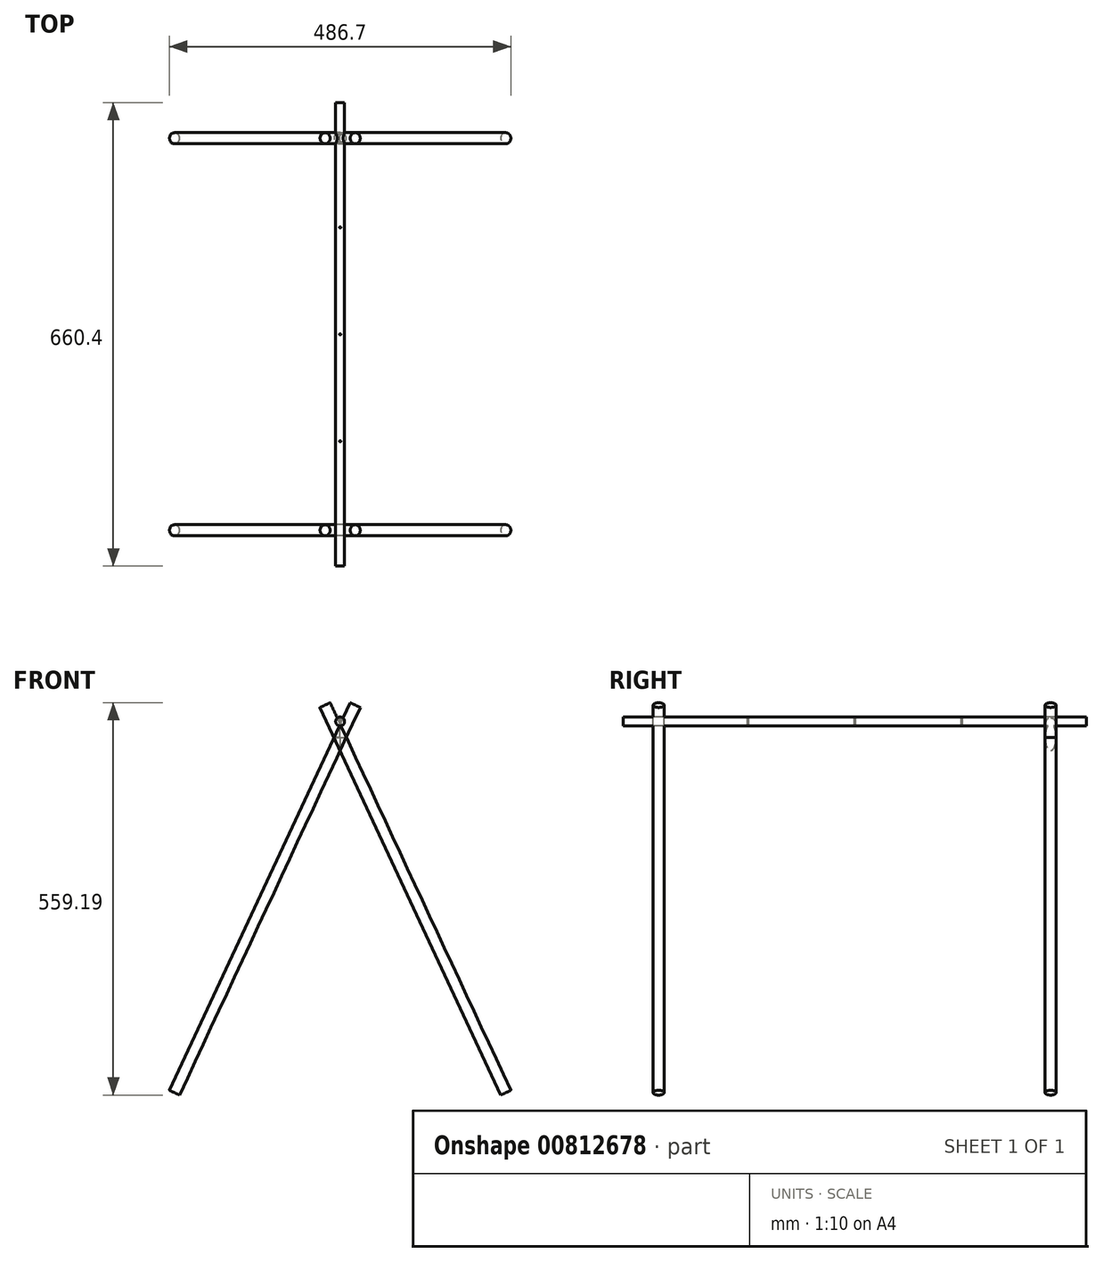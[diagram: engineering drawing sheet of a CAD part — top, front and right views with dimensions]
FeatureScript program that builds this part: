
annotation { "Feature Type Name" : "Feature", "Feature Type Description" : "" }
export const myFeature = defineFeature(function(context is Context, id is Id, definition is map)
    precondition{}
    {
        {
            var Q0;
            Q0=qCreatedBy(makeId("Front.planeOp"),FACE);
            var sketch = newSketch(context, id + "F0", { "sketchPlane" : qUnion([Q0])});
            skLineSegment(sketch, "E0", {"start": v(0, 0) * mm, "end": v(-236.16, -506.44) * mm});
            skLineSegment(sketch, "E1", {"start": v(0, 0) * mm, "end": v(236.16, -506.44) * mm});
            skLineSegment(sketch, "E2", {"start": v(0, 0) * mm, "end": v(21.47, 46.04) * mm});
            skLineSegment(sketch, "E3", {"start": v(0, 0) * mm, "end": v(-21.47, 46.04) * mm});
            skLineSegment(sketch, "E4.0", {"start": v(-7.2, 3.35) * mm, "end": v(-243.35, -503.1) * mm});
            skLineSegment(sketch, "E5.0", {"start": v(-7.2, 3.35) * mm, "end": v(14.28, 49.4) * mm});
            skLineSegment(sketch, "E6", {"start": v(14.28, 49.4) * mm, "end": v(21.47, 46.04) * mm});
            skLineSegment(sketch, "E7", {"start": v(-243.35, -503.1) * mm, "end": v(-236.16, -506.44) * mm});
            skLineSegment(sketch, "E8.0", {"start": v(7.2, 3.35) * mm, "end": v(243.35, -503.1) * mm});
            skLineSegment(sketch, "E9.0", {"start": v(7.2, 3.35) * mm, "end": v(-14.28, 49.4) * mm});
            skLineSegment(sketch, "E10", {"start": v(236.16, -506.44) * mm, "end": v(243.35, -503.1) * mm});
            skLineSegment(sketch, "E11", {"start": v(-21.47, 46.04) * mm, "end": v(-14.28, 49.4) * mm});
            skSolve(sketch);
        }
        {
            var Q0;
            {var subQ0=sQuery(id+"F0.wireOp",EDGE,"E2");Q0=makeQuery(id+"F0.imprint","IMPRINT",FACE,{"disambiguationData":[TD([[makeQuery(id+"F0.imprint","IMPRINT",EDGE,{"derivedFrom":subQ0}),1.0]])]});}
            var Q1;
            {var subQ0=sQuery(id+"F0.wireOp",EDGE,"E5.0");var subQ1=sQuery(id+"F0.wireOp",EDGE,"E4.0");var subQ2=makeQuery(id+"F0.imprint","INTERSECT",VERTEX,{"derivedFrom":[subQ1,subQ0]});Q1=makeQuery(id+"F0.imprint","IMPRINT",FACE,{"disambiguationData":[TD([[makeQuery(id+"F0.imprint","IMPRINT",EDGE,{"disambiguationData":[TD([[subQ2,-1.0]])],"derivedFrom":subQ1}),1.0]])]});}
            var Q2;
            {var subQ7=sQuery(id+"F0.wireOp",EDGE,"E7");Q2=makeQuery(id+"F0.imprint","IMPRINT",FACE,{"disambiguationData":[TD([[makeQuery(id+"F0.imprint","IMPRINT",EDGE,{"derivedFrom":subQ7}),1.0]])]});}
            var Q3;
            Q3=sQuery(id+"F0.wireOp",EDGE,"E0");
            revolve(context, id + "F1", {"surfaceOperationType" : NewSurfaceOperationType.NEW, "entities" : qUnion([Q0, Q1, Q2]), "axis" : qUnion([Q3]), "revolveType" : RevolveType.FULL});
        }
        {
            var Q0;
            {var subQ0=sQuery(id+"F0.wireOp",EDGE,"E11");Q0=makeQuery(id+"F0.imprint","IMPRINT",FACE,{"disambiguationData":[TD([[makeQuery(id+"F0.imprint","IMPRINT",EDGE,{"derivedFrom":subQ0}),-1.0]])]});}
            var Q1;
            {var subQ4=sQuery(id+"F0.wireOp",EDGE,"E1");Q1=makeQuery(id+"F0.imprint","IMPRINT",FACE,{"disambiguationData":[TD([[makeQuery(id+"F0.imprint","IMPRINT",EDGE,{"derivedFrom":subQ4}),1.0]])]});}
            var Q2;
            {var subQ0=sQuery(id+"F0.wireOp",EDGE,"E3");var subQ5=sQuery(id+"F0.wireOp",EDGE,"E5.0");var subQ6=makeQuery(id+"F0.imprint","INTERSECT",VERTEX,{"derivedFrom":[subQ0,subQ5]});Q2=makeQuery(id+"F0.imprint","IMPRINT",FACE,{"disambiguationData":[TD([[makeQuery(id+"F0.imprint","IMPRINT",EDGE,{"disambiguationData":[TD([[subQ6,-1.0]])],"derivedFrom":subQ5}),-1.0]])]});}
            var Q3;
            Q3=sQuery(id+"F0.wireOp",EDGE,"E1");
            revolve(context, id + "F2", {"surfaceOperationType" : NewSurfaceOperationType.NEW, "entities" : qUnion([Q0, Q1, Q2]), "axis" : qUnion([Q3]), "revolveType" : RevolveType.FULL});
        }
        {
            var Q0;
            Q0=qCreatedBy(makeId("Front.planeOp"),FACE);
            var sketch = newSketch(context, id + "F3", { "sketchPlane" : qUnion([Q0])});
            skLineSegment(sketch, "E12.0", {"start": v(7.2, 3.35) * mm, "end": v(-14.28, 49.4) * mm});
            skLineSegment(sketch, "E13.0", {"start": v(-7.2, 3.35) * mm, "end": v(14.28, 49.4) * mm});
            skLineSegment(sketch, "E14.0", {"start": v(0, 0) * mm, "end": v(21.47, 46.04) * mm});
            skLineSegment(sketch, "E15.0", {"start": v(0, 0) * mm, "end": v(-21.47, 46.04) * mm});
            skLineSegment(sketch, "E16", {"start": v(0, 18.78) * mm, "end": v(0, 22.75) * mm});
            skCircle(sketch, "E17", {"center": v(0, 22.75) * mm, "radius": 6.35 * mm});
            skSolve(sketch);
        }
        {
            var Q0;
            {var subQ0=sQuery(id+"F3.wireOp",EDGE,"E13.0");var subQ1=sQuery(id+"F3.wireOp",EDGE,"E12.0");var subQ2=makeQuery(id+"F3.imprint","INTERSECT",VERTEX,{"derivedFrom":[subQ1,subQ0]});Q0=makeQuery(id+"F3.imprint","IMPRINT",FACE,{"disambiguationData":[TD([[makeQuery(id+"F3.imprint","IMPRINT",EDGE,{"disambiguationData":[TD([[subQ2,-1.0]])],"derivedFrom":subQ1}),-1.0]])]});}
            var Q1;
            {var subQ0=sQuery(id+"F3.wireOp",EDGE,"E13.0");var subQ1=sQuery(id+"F3.wireOp",EDGE,"E12.0");var subQ2=makeQuery(id+"F3.imprint","INTERSECT",VERTEX,{"derivedFrom":[subQ1,subQ0]});Q1=makeQuery(id+"F3.imprint","IMPRINT",FACE,{"disambiguationData":[TD([[makeQuery(id+"F3.imprint","IMPRINT",EDGE,{"disambiguationData":[TD([[subQ2,1.0]])],"derivedFrom":subQ1}),-1.0]])]});}
            var Q2;
            {var subQ0=sQuery(id+"F3.wireOp",EDGE,"E13.0");var subQ1=sQuery(id+"F3.wireOp",EDGE,"E12.0");var subQ2=makeQuery(id+"F3.imprint","INTERSECT",VERTEX,{"derivedFrom":[subQ1,subQ0]});Q2=makeQuery(id+"F3.imprint","IMPRINT",FACE,{"disambiguationData":[TD([[makeQuery(id+"F3.imprint","IMPRINT",EDGE,{"disambiguationData":[TD([[subQ2,1.0]])],"derivedFrom":subQ1}),1.0]])]});}
            var Q3;
            {var subQ0=sQuery(id+"F3.wireOp",EDGE,"E13.0");var subQ1=sQuery(id+"F3.wireOp",EDGE,"E12.0");var subQ2=makeQuery(id+"F3.imprint","INTERSECT",VERTEX,{"derivedFrom":[subQ1,subQ0]});Q3=makeQuery(id+"F3.imprint","IMPRINT",FACE,{"disambiguationData":[TD([[makeQuery(id+"F3.imprint","IMPRINT",EDGE,{"disambiguationData":[TD([[subQ2,-1.0]])],"derivedFrom":subQ1}),1.0]])]});}
            extrude(context, id + "F4", {"entities" : qUnion([Q0, Q1, Q2, Q3]), "operationType" : NewBodyOperationType.ADD, "oppositeDirection" : true, "depth" : 50.8 * mm, "offsetDistance" : 25.4 * mm, "hasSecondDirection" : true, "secondDirectionOppositeDirection" : false, "secondDirectionDepth" : 609.6 * mm});
        }
        {
            var Q0;
            Q0=qCreatedBy(makeId("Front.planeOp"),FACE);
            cPlane(context, id + "F5", {"entities" : qUnion([Q0]), "cplaneType" : CPlaneType.OFFSET, "offset" : 558.8 * mm, "width" : 152.4 * mm, "height" : 152.4 * mm});
        }
        {
            var Q0;
            Q0=qCreatedBy(id+"F5.planeOp",FACE);
            var sketch = newSketch(context, id + "F6", { "sketchPlane" : qUnion([Q0])});
            skLineSegment(sketch, "E18", {"start": v(0, 0) * mm, "end": v(-236.16, -506.44) * mm});
            skLineSegment(sketch, "E19", {"start": v(0, 0) * mm, "end": v(236.16, -506.44) * mm});
            skLineSegment(sketch, "E20", {"start": v(0, 0) * mm, "end": v(21.47, 46.04) * mm});
            skLineSegment(sketch, "E21", {"start": v(0, 0) * mm, "end": v(-21.47, 46.04) * mm});
            skLineSegment(sketch, "E22.0", {"start": v(-7.2, 3.35) * mm, "end": v(-243.35, -503.1) * mm});
            skLineSegment(sketch, "E23.0", {"start": v(-7.2, 3.35) * mm, "end": v(14.28, 49.4) * mm});
            skLineSegment(sketch, "E24", {"start": v(14.28, 49.4) * mm, "end": v(21.47, 46.04) * mm});
            skLineSegment(sketch, "E25", {"start": v(-243.35, -503.1) * mm, "end": v(-236.16, -506.44) * mm});
            skLineSegment(sketch, "E26.0", {"start": v(7.2, 3.35) * mm, "end": v(243.35, -503.1) * mm});
            skLineSegment(sketch, "E27.0", {"start": v(7.2, 3.35) * mm, "end": v(-14.28, 49.4) * mm});
            skLineSegment(sketch, "E28", {"start": v(236.16, -506.44) * mm, "end": v(243.35, -503.1) * mm});
            skLineSegment(sketch, "E29", {"start": v(-21.47, 46.04) * mm, "end": v(-14.28, 49.4) * mm});
            skSolve(sketch);
        }
        {
            var Q0;
            {var subQ0=sQuery(id+"F6.wireOp",EDGE,"E29");Q0=makeQuery(id+"F6.imprint","IMPRINT",FACE,{"disambiguationData":[TD([[makeQuery(id+"F6.imprint","IMPRINT",EDGE,{"derivedFrom":subQ0}),-1.0]])]});}
            var Q1;
            {var subQ0=sQuery(id+"F6.wireOp",EDGE,"E21");var subQ5=sQuery(id+"F6.wireOp",EDGE,"E23.0");var subQ6=makeQuery(id+"F6.imprint","INTERSECT",VERTEX,{"derivedFrom":[subQ0,subQ5]});Q1=makeQuery(id+"F6.imprint","IMPRINT",FACE,{"disambiguationData":[TD([[makeQuery(id+"F6.imprint","IMPRINT",EDGE,{"disambiguationData":[TD([[subQ6,-1.0]])],"derivedFrom":subQ5}),-1.0]])]});}
            var Q2;
            {var subQ4=sQuery(id+"F6.wireOp",EDGE,"E19");Q2=makeQuery(id+"F6.imprint","IMPRINT",FACE,{"disambiguationData":[TD([[makeQuery(id+"F6.imprint","IMPRINT",EDGE,{"derivedFrom":subQ4}),1.0]])]});}
            var Q3;
            Q3=sQuery(id+"F6.wireOp",EDGE,"E19");
            revolve(context, id + "F7", {"surfaceOperationType" : NewSurfaceOperationType.NEW, "entities" : qUnion([Q0, Q1, Q2]), "axis" : qUnion([Q3]), "revolveType" : RevolveType.FULL});
        }
        {
            var Q0;
            {var subQ0=sQuery(id+"F6.wireOp",EDGE,"E24");Q0=makeQuery(id+"F6.imprint","IMPRINT",FACE,{"disambiguationData":[TD([[makeQuery(id+"F6.imprint","IMPRINT",EDGE,{"derivedFrom":subQ0}),-1.0]])]});}
            var Q1;
            {var subQ0=sQuery(id+"F6.wireOp",EDGE,"E21");var subQ5=sQuery(id+"F6.wireOp",EDGE,"E23.0");var subQ6=makeQuery(id+"F6.imprint","INTERSECT",VERTEX,{"derivedFrom":[subQ0,subQ5]});Q1=makeQuery(id+"F6.imprint","IMPRINT",FACE,{"disambiguationData":[TD([[makeQuery(id+"F6.imprint","IMPRINT",EDGE,{"disambiguationData":[TD([[subQ6,-1.0]])],"derivedFrom":subQ5}),-1.0]])]});}
            var Q2;
            {var subQ4=sQuery(id+"F6.wireOp",EDGE,"E18");Q2=makeQuery(id+"F6.imprint","IMPRINT",FACE,{"disambiguationData":[TD([[makeQuery(id+"F6.imprint","IMPRINT",EDGE,{"derivedFrom":subQ4}),-1.0]])]});}
            var Q3;
            Q3=sQuery(id+"F6.wireOp",EDGE,"E18");
            revolve(context, id + "F8", {"surfaceOperationType" : NewSurfaceOperationType.NEW, "entities" : qUnion([Q0, Q1, Q2]), "axis" : qUnion([Q3]), "revolveType" : RevolveType.FULL});
        }
        {
            var Q0;
            Q0=qCreatedBy(makeId("Top.planeOp"),FACE);
            var sketch = newSketch(context, id + "F9", { "sketchPlane" : qUnion([Q0])});
            skLineSegment(sketch, "E30", {"start": v(6.35, 50.8) * mm, "end": v(6.35, -609.6) * mm});
            skLineSegment(sketch, "E31", {"start": v(-6.35, -609.6) * mm, "end": v(-6.35, 50.8) * mm});
            skLineSegment(sketch, "E32.0", {"start": v(6.35, 50.8) * mm, "end": v(-6.35, 50.8) * mm});
            skLineSegment(sketch, "E33.0", {"start": v(6.35, -609.6) * mm, "end": v(-6.35, -609.6) * mm});
            skLineSegment(sketch, "E34", {"start": v(236.16, -7.94) * mm, "end": v(0, -7.94) * mm});
            skLineSegment(sketch, "E35", {"start": v(-21.47, -550.86) * mm, "end": v(236.16, -550.86) * mm});
            skLineSegment(sketch, "E36", {"start": v(0, -609.6) * mm, "end": v(0, 50.8) * mm, "construction": true});
            skCircle(sketch, "E37", {"center": v(0, -279.4) * mm, "radius": 0.8 * mm});
            skLineSegment(sketch, "E38", {"start": v(0, -279.4) * mm, "end": v(0, -127) * mm, "construction": true});
            skLineSegment(sketch, "E39", {"start": v(0, -279.4) * mm, "end": v(0, -431.8) * mm, "construction": true});
            skCircle(sketch, "E40", {"center": v(0, -431.8) * mm, "radius": 0.8 * mm});
            skCircle(sketch, "E41", {"center": v(0, -127) * mm, "radius": 0.8 * mm});
            skSolve(sketch);
        }
        {
            var Q0;
            Q0=sQuery(id+"F9.wireOp",VERTEX,"E38.end");
            var Q1;
            Q1=sQuery(id+"F9.wireOp",VERTEX,"E38.start");
            var Q2;
            Q2=sQuery(id+"F9.wireOp",VERTEX,"E39.end");
            var Q3;
            Q3=makeQuery(id+"F1.opRevolve","SWEPT_BODY",BODY,{"disambiguationData":[OSD([sQuery(id+"F0.wireOp",EDGE,"E0"),sQuery(id+"F0.wireOp",EDGE,"E2"),sQuery(id+"F0.wireOp",EDGE,"E4.0"),sQuery(id+"F0.wireOp",EDGE,"E5.0"),sQuery(id+"F0.wireOp",EDGE,"E6"),sQuery(id+"F0.wireOp",EDGE,"E7")])]});
            hole(context, id + "F10", {"style" : HoleStyle.SIMPLE, "endStyle" : HoleEndStyle.THROUGH, "oppositeDirection" : true, "holeDiameter" : 1.59 * mm, "majorDiameter" : 6.35 * mm, "isTappedThrough" : true, "tappedDepth" : 12.7 * mm, "tapClearance" : 3, "locations" : qUnion([Q0, Q1, Q2]), "scope" : qUnion([Q3])});
        }
    });
